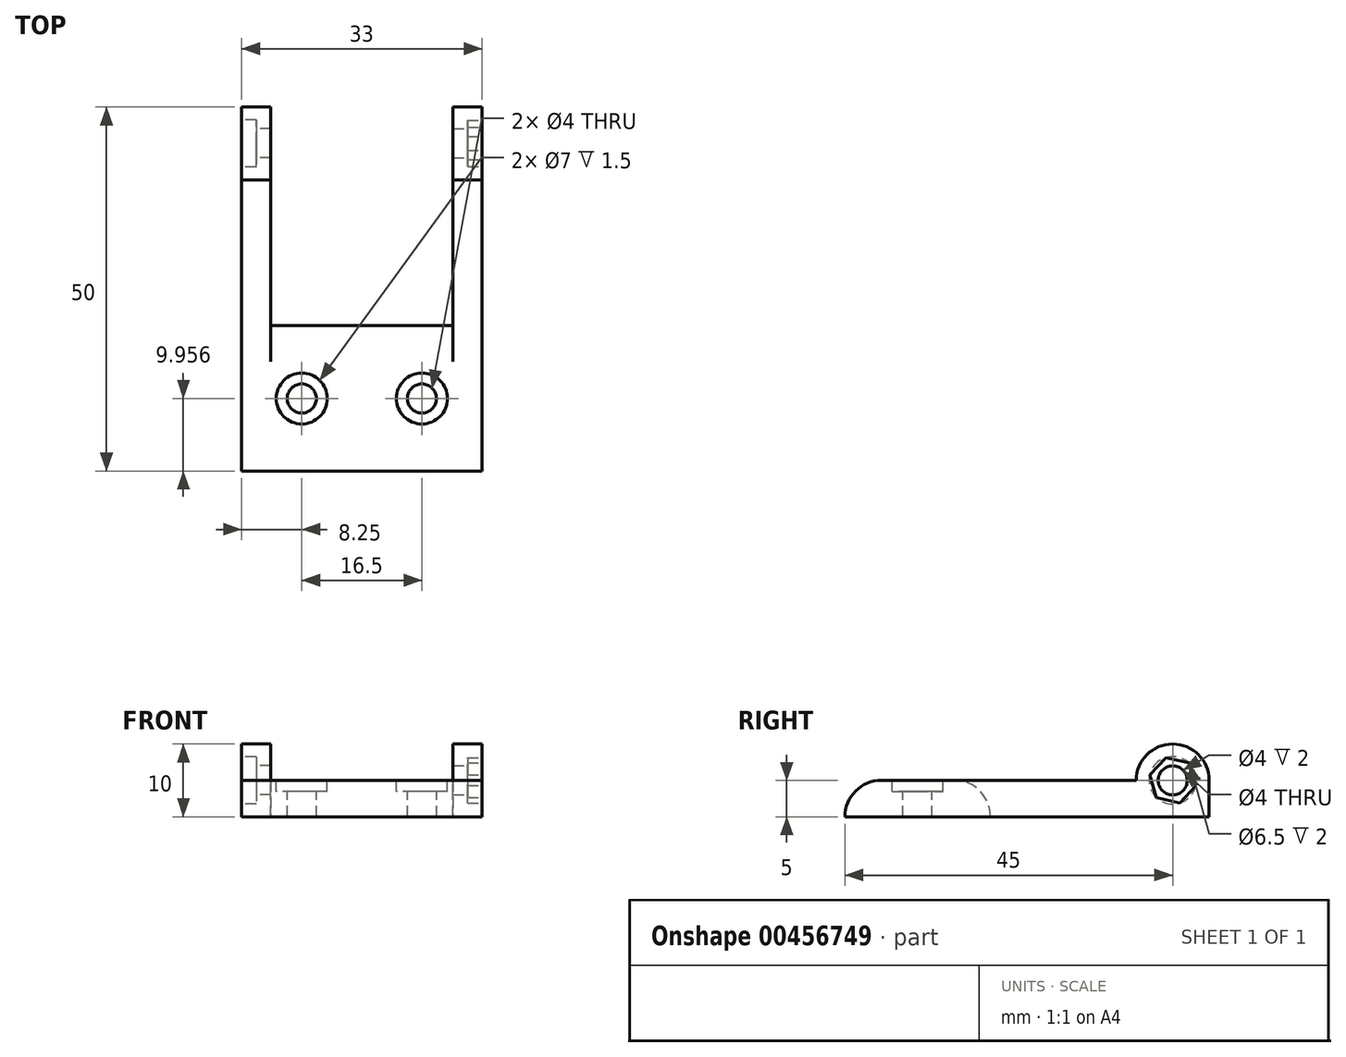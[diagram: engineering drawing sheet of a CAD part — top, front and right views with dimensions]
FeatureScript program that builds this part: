
annotation { "Feature Type Name" : "Feature", "Feature Type Description" : "" }
export const myFeature = defineFeature(function(context is Context, id is Id, definition is map)
    precondition{}
    {
        {
            var Q0;
            Q0=qCreatedBy(makeId("Top.planeOp"),FACE);
            var sketch = newSketch(context, id + "F0", { "sketchPlane" : qUnion([Q0])});
            skLineSegment(sketch, "E0.bottom", {"start": v(16.5, 25) * mm, "end": v(12.5, 25) * mm});
            skLineSegment(sketch, "E0.top", {"start": v(16.5, -25) * mm, "end": v(-16.5, -25) * mm});
            skLineSegment(sketch, "E0.left", {"start": v(16.5, 25) * mm, "end": v(16.5, -25) * mm});
            skLineSegment(sketch, "E0.right", {"start": v(-16.5, 25) * mm, "end": v(-16.5, -25) * mm});
            skPoint(sketch, "E0.middle", {"position": v(0, 0) * mm});
            skLineSegment(sketch, "E1.top", {"start": v(-12.5, -5) * mm, "end": v(12.5, -5) * mm});
            skLineSegment(sketch, "E1.left", {"start": v(-12.5, 25) * mm, "end": v(-12.5, -5) * mm});
            skLineSegment(sketch, "E1.right", {"start": v(12.5, 25) * mm, "end": v(12.5, -5) * mm});
            skLineSegment(sketch, "E2.trimOffspring", {"start": v(-12.5, 25) * mm, "end": v(-16.5, 25) * mm});
            skSolve(sketch);
        }
        {
            var Q0;
            Q0=makeQuery(id+"F0.imprint","IMPRINT",FACE,{"disambiguationData":[TD([[makeQuery(id+"F0.imprint","IMPRINT",EDGE,{"derivedFrom":sQuery(id+"F0.wireOp",EDGE,"E0.bottom")}),1.0]])]});
            extrude(context, id + "F1", {"entities" : qUnion([Q0]), "depth" : 5 * mm});
        }
        {
            var Q0;
            Q0=makeQuery(id+"F1.opExtrude","SWEPT_FACE",FACE,{"disambiguationData":[OSD([sQuery(id+"F0.wireOp",EDGE,"E0.right")])]});
            var sketch = newSketch(context, id + "F2", { "sketchPlane" : qUnion([Q0])});
            skLineSegment(sketch, "E3.bottom", {"start": v(-25, 0) * mm, "end": v(-15, 0) * mm});
            skLineSegment(sketch, "E3.top", {"start": v(-25, 10) * mm, "end": v(-15, 10) * mm});
            skLineSegment(sketch, "E3.left", {"start": v(-25, 0) * mm, "end": v(-25, 10) * mm});
            skLineSegment(sketch, "E3.right", {"start": v(-15, 0) * mm, "end": v(-15, 10) * mm});
            skSolve(sketch);
        }
        {
            var Q0;
            Q0 = qSketchRegion(id + "F2", true);
            var Q1;
            Q1=sQuery(id+"F2.wireOp",VERTEX,"E3.left.end");
            extrude(context, id + "F3", {"entities" : qUnion([Q0]), "operationType" : NewBodyOperationType.ADD, "oppositeDirection" : true, "endBoundEntityVertex" : qUnion([Q1]), "depth" : 4 * mm});
        }
        {
            var Q0;
            Q0=makeQuery(id+"F3.boolean.opBoolean","MERGE",FACE,{"derivedFrom":[makeQuery(id+"F1.opExtrude","SWEPT_FACE",FACE,{"disambiguationData":[OSD([sQuery(id+"F0.wireOp",EDGE,"E0.right")])]}),makeQuery(id+"F3.opExtrude","CAP_FACE",FACE,{"disambiguationData":[OSD([sQuery(id+"F2.wireOp",EDGE,"E3.bottom"),sQuery(id+"F2.wireOp",EDGE,"E3.top"),sQuery(id+"F2.wireOp",EDGE,"E3.left"),sQuery(id+"F2.wireOp",EDGE,"E3.right")])],"isStart":true})]});
            var sketch = newSketch(context, id + "F4", { "sketchPlane" : qUnion([Q0])});
            skLineSegment(sketch, "E4", {"start": v(-20, 0) * mm, "end": v(-20, 10) * mm, "construction": true});
            skLineSegment(sketch, "E5", {"start": v(-15, 5) * mm, "end": v(-25, 5) * mm, "construction": true});
            skPoint(sketch, "E6", {"position": v(-20, 5) * mm});
            skSolve(sketch);
        }
        {
            var Q0;
            Q0=sQuery(id+"F4.wireOp",VERTEX,"E6");
            var Q1;
            Q1=makeQuery(id+"F1.opExtrude","SWEPT_BODY",BODY,{"disambiguationData":[OSD([sQuery(id+"F0.wireOp",EDGE,"E0.bottom"),sQuery(id+"F0.wireOp",EDGE,"E0.top"),sQuery(id+"F0.wireOp",EDGE,"E0.left"),sQuery(id+"F0.wireOp",EDGE,"E0.right"),sQuery(id+"F0.wireOp",EDGE,"E1.top"),sQuery(id+"F0.wireOp",EDGE,"E1.left"),sQuery(id+"F0.wireOp",EDGE,"E1.right"),sQuery(id+"F0.wireOp",EDGE,"E2.trimOffspring")])]});
            hole(context, id + "F5", {"style" : HoleStyle.C_BORE, "endStyle" : HoleEndStyle.THROUGH, "holeDiameter" : 4 * mm, "cBoreDiameter" : 6.5 * mm, "cBoreDepth" : 2 * mm, "isTappedThrough" : true, "tappedDepth" : 12 * mm, "tapClearance" : 3, "startFromSketch" : true, "locations" : qUnion([Q0]), "scope" : qUnion([Q1])});
        }
        {
            var Q0;
            Q0=makeQuery(id+"F1.opExtrude","SWEPT_FACE",FACE,{"disambiguationData":[OSD([sQuery(id+"F0.wireOp",EDGE,"E0.left")])]});
            var sketch = newSketch(context, id + "F6", { "sketchPlane" : qUnion([Q0])});
            skLineSegment(sketch, "E7.0.0", {"start": v(25, 0) * mm, "end": v(-25, 0) * mm});
            skLineSegment(sketch, "E7.0.1", {"start": v(-25, 0) * mm, "end": v(-25, 5) * mm});
            skLineSegment(sketch, "E7.0.2", {"start": v(-25, 5) * mm, "end": v(15, 5) * mm});
            skLineSegment(sketch, "E7.0.3", {"start": v(15, 5) * mm, "end": v(15, 10) * mm});
            skLineSegment(sketch, "E7.0.4", {"start": v(15, 10) * mm, "end": v(25, 10) * mm});
            skLineSegment(sketch, "E7.0.5", {"start": v(25, 10) * mm, "end": v(25, 0) * mm});
            skSolve(sketch);
        }
        {
            var Q0;
            {var subQ11=sQuery(id+"F6.wireOp",EDGE,"E7.0.3");Q0=makeQuery(id+"F6.imprint","IMPRINT",FACE,{"disambiguationData":[TD([[makeQuery(id+"F6.imprint","IMPRINT",EDGE,{"derivedFrom":subQ11}),-1.0]])]});}
            extrude(context, id + "F7", {"entities" : qUnion([Q0]), "operationType" : NewBodyOperationType.ADD, "oppositeDirection" : true, "depth" : 4 * mm});
        }
        {
            var Q0;
            {var subQ0=sQuery(id+"F0.wireOp",EDGE,"E0.left");Q0=makeQuery(id+"F7.boolean.opBoolean","MERGE",FACE,{"derivedFrom":[makeQuery(id+"F1.opExtrude","SWEPT_FACE",FACE,{"disambiguationData":[OSD([subQ0])]}),makeQuery(id+"F7.opExtrude","CAP_FACE",FACE,{"disambiguationData":[OSD([subQ0,sQuery(id+"F5.hole-0.sketch.wireOp",EDGE,"core_line_2"),sQuery(id+"F6.wireOp",EDGE,"E7.0.3"),sQuery(id+"F6.wireOp",EDGE,"E7.0.4"),sQuery(id+"F6.wireOp",EDGE,"E7.0.5")])],"isStart":true})]});}
            var sketch = newSketch(context, id + "F8", { "sketchPlane" : qUnion([Q0])});
            skLineSegment(sketch, "E8", {"start": v(20, 10) * mm, "end": v(20, 0) * mm, "construction": true});
            skLineSegment(sketch, "E9", {"start": v(15, 5) * mm, "end": v(25, 5) * mm, "construction": true});
            skPoint(sketch, "E10", {"position": v(20, 5) * mm});
            skSolve(sketch);
        }
        {
            var Q0;
            Q0=sQuery(id+"F8.wireOp",VERTEX,"E10");
            var Q1;
            Q1=makeQuery(id+"F1.opExtrude","SWEPT_BODY",BODY,{"disambiguationData":[OSD([sQuery(id+"F0.wireOp",EDGE,"E0.bottom"),sQuery(id+"F0.wireOp",EDGE,"E0.top"),sQuery(id+"F0.wireOp",EDGE,"E0.left"),sQuery(id+"F0.wireOp",EDGE,"E0.right"),sQuery(id+"F0.wireOp",EDGE,"E1.top"),sQuery(id+"F0.wireOp",EDGE,"E1.left"),sQuery(id+"F0.wireOp",EDGE,"E1.right"),sQuery(id+"F0.wireOp",EDGE,"E2.trimOffspring")])]});
            hole(context, id + "F9", {"style" : HoleStyle.SIMPLE, "endStyle" : HoleEndStyle.THROUGH, "holeDiameter" : 4 * mm, "isTappedThrough" : true, "tappedDepth" : 12 * mm, "tapClearance" : 3, "startFromSketch" : true, "locations" : qUnion([Q0]), "scope" : qUnion([Q1])});
        }
        {
            var Q0;
            {var subQ0=sQuery(id+"F0.wireOp",EDGE,"E0.left");Q0=makeQuery(id+"F7.boolean.opBoolean","MERGE",FACE,{"derivedFrom":[makeQuery(id+"F1.opExtrude","SWEPT_FACE",FACE,{"disambiguationData":[OSD([subQ0])]}),makeQuery(id+"F7.opExtrude","CAP_FACE",FACE,{"disambiguationData":[OSD([subQ0,sQuery(id+"F5.hole-0.sketch.wireOp",EDGE,"core_line_2"),sQuery(id+"F6.wireOp",EDGE,"E7.0.3"),sQuery(id+"F6.wireOp",EDGE,"E7.0.4"),sQuery(id+"F6.wireOp",EDGE,"E7.0.5")])],"isStart":true})]});}
            var sketch = newSketch(context, id + "F10", { "sketchPlane" : qUnion([Q0])});
            skCircle(sketch, "E11.0", {"center": v(20, 5) * mm, "radius": 2 * mm});
            skCircle(sketch, "E12.cCircle", {"center": v(20, 5) * mm, "radius": 2.83 * mm, "construction": true});
            skLineSegment(sketch, "E12.0", {"start": v(23.18, 4.26) * mm, "end": v(20.95, 1.88) * mm});
            skLineSegment(sketch, "E12.1", {"start": v(20.95, 1.88) * mm, "end": v(17.77, 2.62) * mm});
            skLineSegment(sketch, "E12.2", {"start": v(17.77, 2.62) * mm, "end": v(16.82, 5.74) * mm});
            skLineSegment(sketch, "E12.3", {"start": v(16.82, 5.74) * mm, "end": v(19.05, 8.12) * mm});
            skLineSegment(sketch, "E12.4", {"start": v(19.05, 8.12) * mm, "end": v(22.23, 7.38) * mm});
            skLineSegment(sketch, "E12.5", {"start": v(22.23, 7.38) * mm, "end": v(23.18, 4.26) * mm});
            skPoint(sketch, "E12.0.midPoint", {"position": v(22.06, 3.07) * mm});
            skSolve(sketch);
        }
        {
            var Q0;
            Q0=makeQuery(id+"F10.imprint","IMPRINT",FACE,{"disambiguationData":[TD([[makeQuery(id+"F10.imprint","IMPRINT",EDGE,{"derivedFrom":sQuery(id+"F10.wireOp",EDGE,"E11.0")}),-1.0]])]});
            extrude(context, id + "F11", {"entities" : qUnion([Q0]), "operationType" : NewBodyOperationType.REMOVE, "oppositeDirection" : true, "depth" : 2 * mm});
        }
        {
            var Q0;
            Q0=makeQuery(id+"F7.opExtrude","SWEPT_EDGE",EDGE,{"disambiguationData":[OSD([sQuery(id+"F6.wireOp",EDGE,"E7.0.4"),sQuery(id+"F6.wireOp",EDGE,"E7.0.5")])]});
            var Q1;
            Q1=makeQuery(id+"F7.opExtrude","SWEPT_EDGE",EDGE,{"disambiguationData":[OSD([sQuery(id+"F6.wireOp",EDGE,"E7.0.3"),sQuery(id+"F6.wireOp",EDGE,"E7.0.4")])]});
            var Q2;
            Q2=makeQuery(id+"F3.opExtrude","SWEPT_EDGE",EDGE,{"disambiguationData":[OSD([sQuery(id+"F2.wireOp",EDGE,"E3.top"),sQuery(id+"F2.wireOp",EDGE,"E3.right")])]});
            var Q3;
            Q3=makeQuery(id+"F3.opExtrude","SWEPT_EDGE",EDGE,{"disambiguationData":[OSD([sQuery(id+"F2.wireOp",EDGE,"E3.top"),sQuery(id+"F2.wireOp",EDGE,"E3.left")])]});
            var Q4;
            Q4=makeQuery(id+"F1.opExtrude","CAP_EDGE",EDGE,{"disambiguationData":[OSD([sQuery(id+"F0.wireOp",EDGE,"E0.top")])],"isStart":false});
            var Q5;
            Q5=makeQuery(id+"F1.opExtrude","CAP_EDGE",EDGE,{"disambiguationData":[OSD([sQuery(id+"F0.wireOp",EDGE,"E1.top")])],"isStart":false});
            fillet(context, id + "F12", {"entities" : qUnion([Q0, Q1, Q2, Q3, Q4, Q5]), "radius" : 5 * mm, "tangentPropagation" : true, "allowEdgeOverflow" : false});
        }
        {
            var Q0;
            {var subQ0=sQuery(id+"F0.wireOp",EDGE,"E1.top");var subQ2=sQuery(id+"F0.wireOp",EDGE,"E0.right");var subQ3=sQuery(id+"F0.wireOp",EDGE,"E0.left");var subQ4=sQuery(id+"F0.wireOp",EDGE,"E0.top");var subQ8=sQuery(id+"F0.wireOp",EDGE,"E1.left");var subQ9=sQuery(id+"F0.wireOp",EDGE,"E1.right");Q0=makeQuery(id+"F5.hole-0.boolean.opBoolean","SPLIT",FACE,{"disambiguationData":[TD([makeQuery(id+"F1.opExtrude","SWEPT_FACE",FACE,{"disambiguationData":[OSD([subQ4])]})])],"derivedFrom":makeQuery(id+"F1.opExtrude","CAP_FACE",FACE,{"disambiguationData":[OSD([sQuery(id+"F0.wireOp",EDGE,"E0.bottom"),subQ4,subQ3,subQ2,subQ0,subQ8,subQ9,sQuery(id+"F0.wireOp",EDGE,"E2.trimOffspring")])],"isStart":false})});}
            var sketch = newSketch(context, id + "F13", { "sketchPlane" : qUnion([Q0])});
            skPoint(sketch, "E13", {"position": v(-8.25, -15.04) * mm});
            skPoint(sketch, "E14", {"position": v(8.25, -15.04) * mm});
            skLineSegment(sketch, "E15", {"start": v(-16.5, -15.04) * mm, "end": v(0, -15.04) * mm, "construction": true});
            skLineSegment(sketch, "E16", {"start": v(0, -15.04) * mm, "end": v(16.5, -15.04) * mm, "construction": true});
            skSolve(sketch);
        }
        {
            var Q0;
            Q0=sQuery(id+"F13.wireOp",VERTEX,"E13");
            var Q1;
            Q1=sQuery(id+"F13.wireOp",VERTEX,"E14");
            var Q2;
            Q2=makeQuery(id+"F1.opExtrude","SWEPT_BODY",BODY,{"disambiguationData":[OSD([sQuery(id+"F0.wireOp",EDGE,"E0.bottom"),sQuery(id+"F0.wireOp",EDGE,"E0.top"),sQuery(id+"F0.wireOp",EDGE,"E0.left"),sQuery(id+"F0.wireOp",EDGE,"E0.right"),sQuery(id+"F0.wireOp",EDGE,"E1.top"),sQuery(id+"F0.wireOp",EDGE,"E1.left"),sQuery(id+"F0.wireOp",EDGE,"E1.right"),sQuery(id+"F0.wireOp",EDGE,"E2.trimOffspring")])]});
            hole(context, id + "F14", {"style" : HoleStyle.C_BORE, "endStyle" : HoleEndStyle.THROUGH, "holeDiameter" : 4 * mm, "cBoreDiameter" : 7 * mm, "cBoreDepth" : 1.5 * mm, "isTappedThrough" : true, "tappedDepth" : 12 * mm, "tapClearance" : 3, "startFromSketch" : true, "locations" : qUnion([Q0, Q1]), "scope" : qUnion([Q2])});
        }
    });
